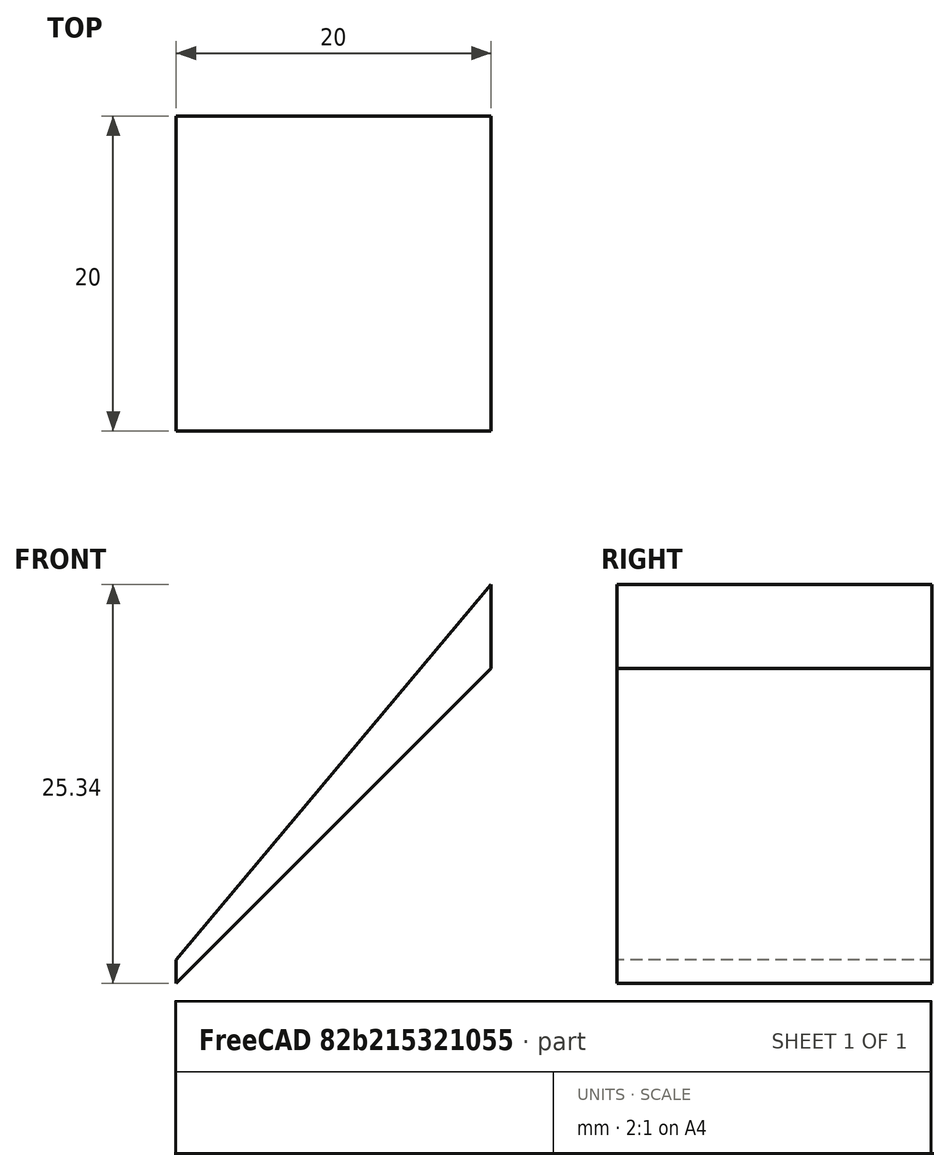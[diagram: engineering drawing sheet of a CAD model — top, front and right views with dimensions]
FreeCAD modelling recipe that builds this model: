
FCSTD DOCUMENT  (FreeCAD 0.15R4641 (Git))
Label: bish-v001b
License: All rights reserved
LicenseURL: http://en.wikipedia.org/wiki/All_rights_reserved
objects: Sketcher::SketchObject×1, PartDesign::Pad×1
note: 3 computed .brp shape members not serialized (recipe doc carries the construction recipe); baked Part::Feature solids carry a one-line shape summary decoded from their .brp

FEATURE [Sketcher::SketchObject] Sketch
  Placement = pos=(0,0,0) rot=(-1,0,0;4.71239rad)
  sketch-geometry (5):
    g0: LineSegment [constr] StartX=0 StartY=0 StartZ=0 EndX=0 EndY=26 EndZ=0
    g1: LineSegment StartX=0 StartY=26 StartZ=0 EndX=0 EndY=27.5 EndZ=0
    g2: LineSegment StartX=0 StartY=27.5 StartZ=0 EndX=20 EndY=51.3351 EndZ=0
    g3: LineSegment StartX=20 StartY=51.3351 StartZ=0 EndX=20 EndY=46 EndZ=0
    g4: LineSegment StartX=20 StartY=46 StartZ=0 EndX=0 EndY=26 EndZ=0
  constraints (14):
    c: Coincident(g0,g-1)
    c: PointOnObject(g0,g-2)
    c: DistanceY(g0) = 26
    c: Coincident(g0,g1)
    c: PointOnObject(g1,g-2)
    c: Coincident(g1,g2)
    c: Coincident(g2,g3)
    c: Coincident(g3,g4)
    c: Coincident(g4,g1)
    c: Vertical(g3)
    c: Angle(g4,g1) = 0.785398
    c: Angle(g1,g2) = 2.44346
    c: DistanceY(g1,g0) = -1.5
    c: DistanceX(g3,g1) = -20
FEATURE [PartDesign::Pad] Pad
  Length = 20
  Length2 = 100
  Midplane = true
  Placement = pos=(0,0,0) rot=(-1,0,0;4.71239rad)
  Sketch = -> Sketch
  Type = 0
